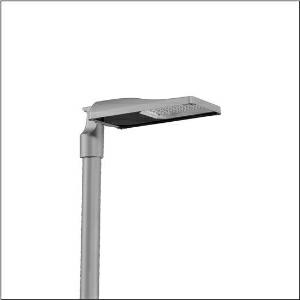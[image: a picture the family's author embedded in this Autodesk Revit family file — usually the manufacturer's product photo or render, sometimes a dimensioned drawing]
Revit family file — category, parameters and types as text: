
# Revit family: streetlight_sl_31_mini___st1_0a_5xh2d3ab08ha_5839
name_source: partatom
category: Lighting Fixtures
units: mm (PartAtom-declared; Revit-internal decimal feet)

## family parameters
Cut with Voids When Loaded = No
Host = Face
Light Source = No
Part Type = Normal
Room Calculation Point = No
Round Connector Dimension = Use Diameter
Shared = No

## types (1)
- --- (1 x LED, 9240 lm, 68.3 W, 3000K)
    Apparent Load = 68 VA
    CIE Flux Codes = 37 72 97 100 100
    Color Rendering = 70
    Color Temperature = 3000K
    Default Elevation = 1800 mm
    Description = Streetlight SL 31 mini Easy LST mast luminaire for post-top, side-entry; light control with lens of PMMA; light distribution: ST1.0a, direct asymmetric distribution, for standard-compliant lighting for roads and squares; LED: luminous flux: 9.240lm, light colour: 730, colour temperature: 3000K; luminous efficacy: 135,3lm/W; control: pre-setting: linear dimming characteristic, flexible luminous flux parameterisation, time-dependent luminous flux control, constant luminous flux control, power reduction, intelligent temperature release in ECG and LED module, overheat protection; luminaire housing, of diecast aluminium, Siteco® metallic grey (DB 702S), corrosivity category C5 high according to DIN EN ISO 12944; cover of toughened safety glass, transparent, mast flange of diecast aluminium, Siteco® metallic grey (DB 702S), spigot size: 76/60mm, mast flange included unmounted; with cable H07RN-F 3x 1.5mm², cable length: 8,5m, connection cable pre-assembled; mains connection: 220..240V, AC, 50/60Hz; power consumption (at start of service life): 68,3W / (at end of service life): 74,8W / (with reduced operation 50%): 29,7W; protection rating (complete): IP66; insulation class (complete): insulation class II (safety insulation); impact resistance: IK10; certification: CE, ENEC, ENEC+, VDE, UKCA; permissible operating ambient temperature for outdoor applications: -40..+50°C; packaging unit: 1 piece

Light Distribution: ST1.0a
    Height = 76 mm
    Lamp = 1 x LED
    Lamp Light Flux = 9240 lm
    Lamp Power = 68.3 W
    Lamp count = 1
    Length = 547 mm
    Luminous efficacy = 135 lm/W
    Manufacturer = Siteco
    ModVariant = No
    Model = 5XH2D3AB08HA
    Number of Poles = 1
    OnlyDefault = Yes
    Power Factor = 1
    Product Name = Streetlight SL 31 mini | ST1.0a
    Product group = mast luminaire | pylon top
    ProductGroupID = 6100
    Protection Class = Protection class II
    Protection Degree = IP 66
    RLX_Detail_Level = 1
    RLX_Emergency_Light_Flux = 0 lm
    RLX_Emergency_Type = 0
    RLX_Emergency_Type_DB = No
    RlxData = <blob elided: 39313 chars, md5=fb055de1>
    Socket = socket
    Standby Power = 0 W
    System Light Flux = 9240 lm
    System Power = 68 W
    Type Comments = factory setting: luminous flux: 100 % | dim-lin: 254 | 693 mA
    Type Image = l_1300326.jpg
    URL = http://relux.com
    VarID = @adj_054944
    Voltage = 0 V
    Weight = 0.00 kg
    Width = 265 mm

## geometry (parser evidence)
native form markers: Blend x4, Sweep x9
no freeform markers — native parametric forms only
